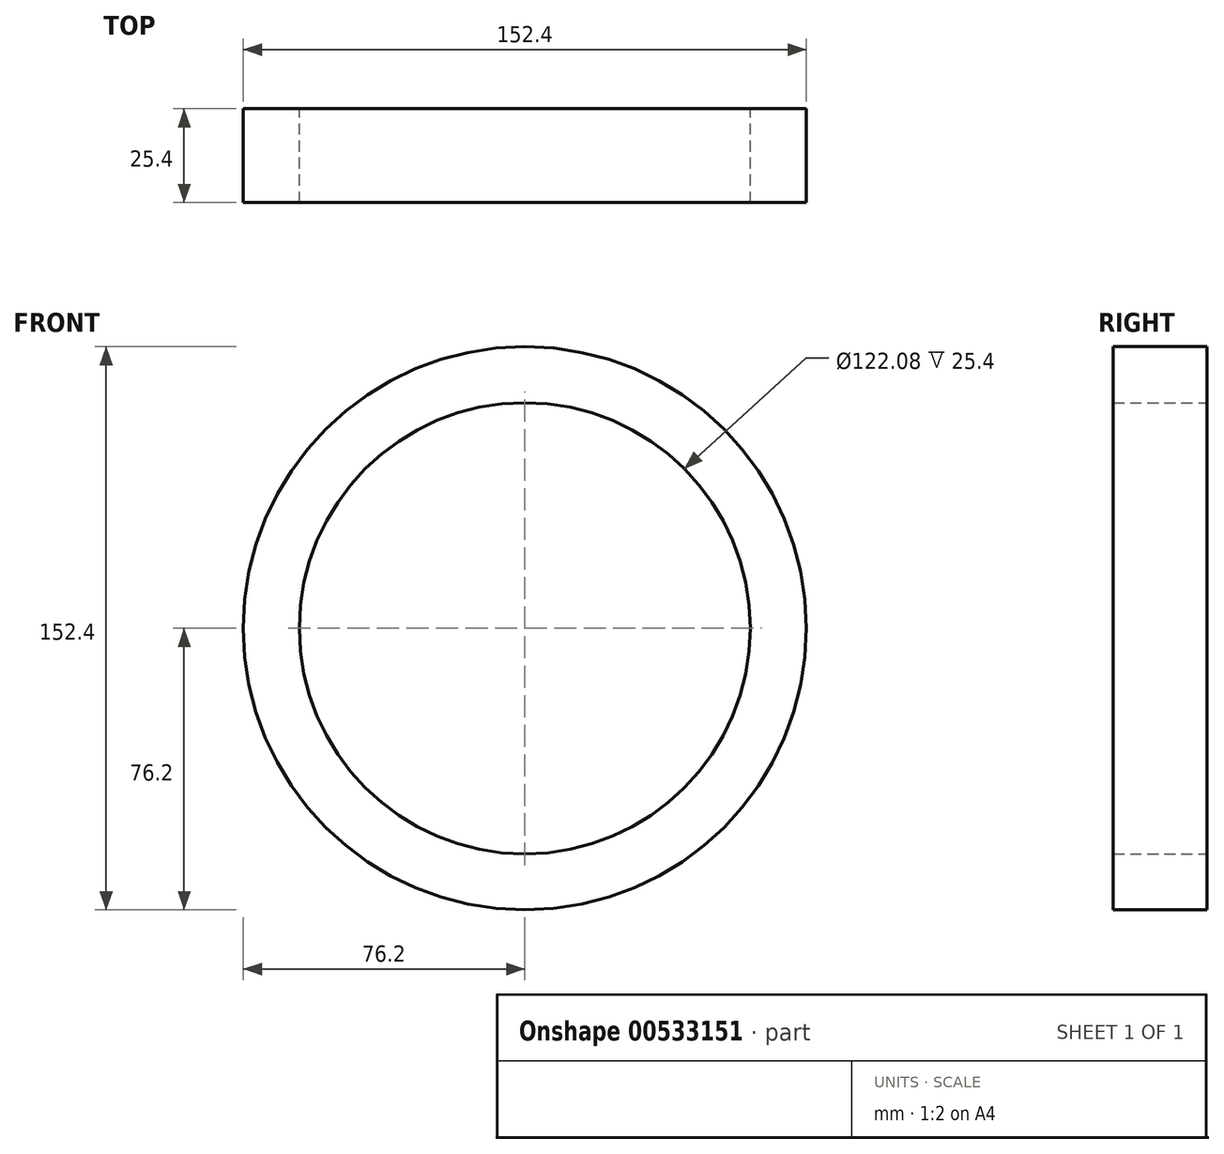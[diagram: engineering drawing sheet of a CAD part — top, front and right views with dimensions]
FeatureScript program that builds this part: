
annotation { "Feature Type Name" : "Feature", "Feature Type Description" : "" }
export const myFeature = defineFeature(function(context is Context, id is Id, definition is map)
    precondition{}
    {
        {
            var Q0;
            Q0=qCreatedBy(makeId("Front.planeOp"),FACE);
            var sketch = newSketch(context, id + "F0", { "sketchPlane" : qUnion([Q0])});
            skCircle(sketch, "E0", {"center": v(0, 0) * mm, "radius": 76.2 * mm});
            skCircle(sketch, "E1", {"center": v(0, 0) * mm, "radius": 61.04 * mm});
            skSolve(sketch);
        }
        {
            var Q0;
            Q0=makeQuery(id+"F0.imprint","IMPRINT",FACE,{"disambiguationData":[TD([[makeQuery(id+"F0.imprint","IMPRINT",EDGE,{"derivedFrom":sQuery(id+"F0.wireOp",EDGE,"E0")}),1.0]])]});
            extrude(context, id + "F1", {"entities" : qUnion([Q0]), "depth" : 25.4 * mm, "offsetDistance" : 25.4 * mm});
        }
    });
